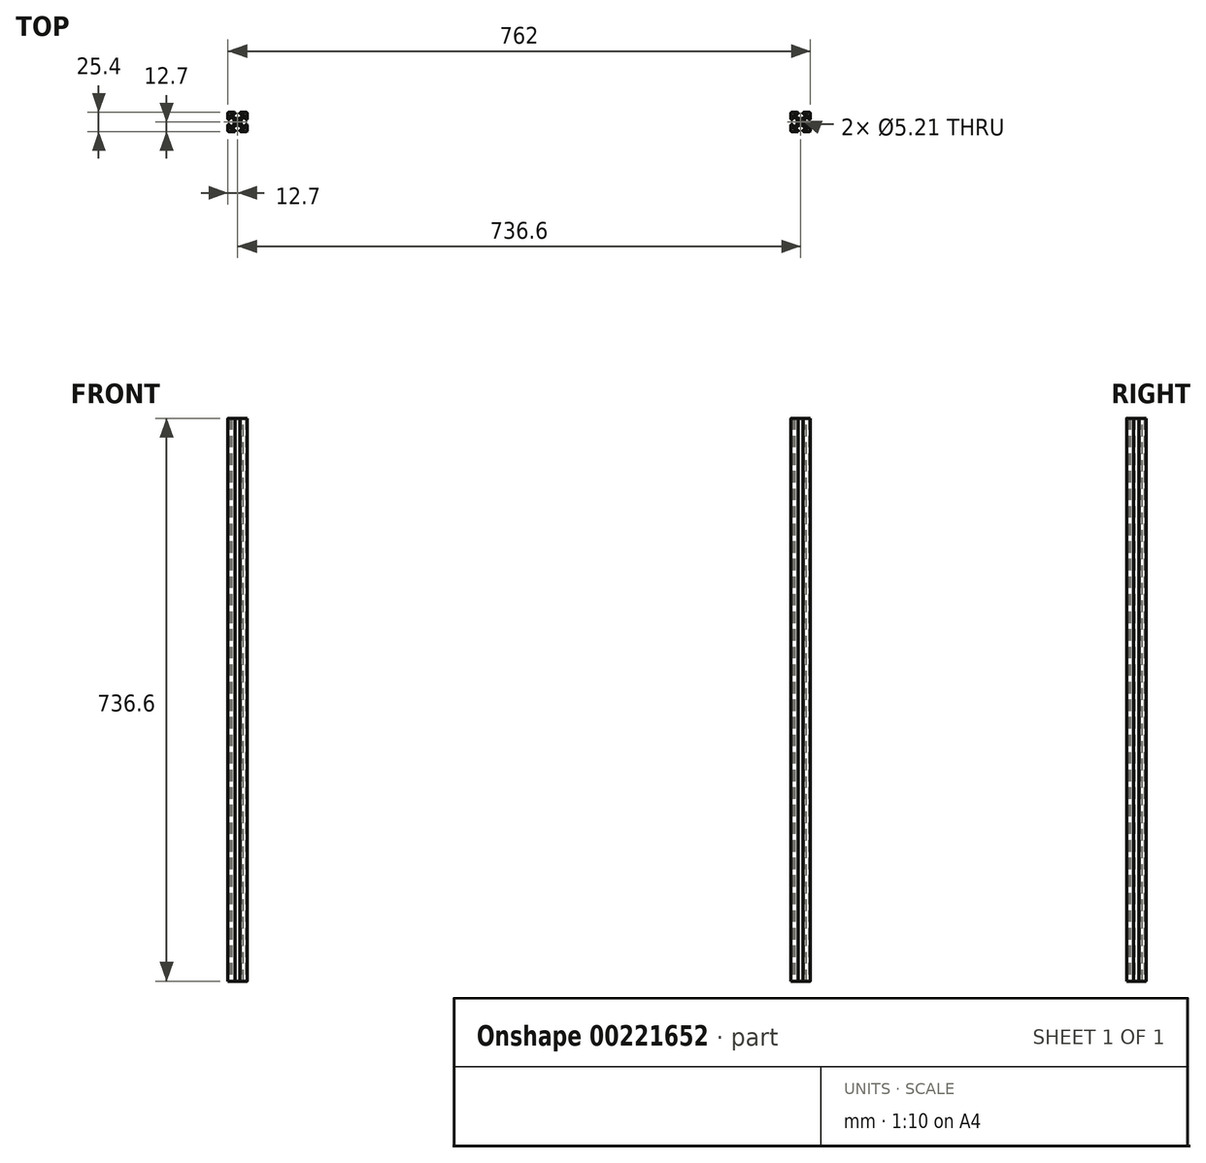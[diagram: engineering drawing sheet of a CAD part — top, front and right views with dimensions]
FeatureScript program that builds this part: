
annotation { "Feature Type Name" : "Feature", "Feature Type Description" : "" }
export const myFeature = defineFeature(function(context is Context, id is Id, definition is map)
    precondition{}
    {
        {
            var Q0;
            Q0=qCreatedBy(makeId("Top.planeOp"),FACE);
            var sketch = newSketch(context, id + "F0", { "sketchPlane" : qUnion([Q0])});
            skLineSegment(sketch, "E0.bottom", {"start": v(12.7, 12.7) * mm, "end": v(-12.7, 12.7) * mm});
            skLineSegment(sketch, "E0.top", {"start": v(12.7, -12.7) * mm, "end": v(-12.7, -12.7) * mm});
            skLineSegment(sketch, "E0.left", {"start": v(12.7, 12.7) * mm, "end": v(12.7, -12.7) * mm});
            skLineSegment(sketch, "E0.right", {"start": v(-12.7, 12.7) * mm, "end": v(-12.7, -12.7) * mm});
            skPoint(sketch, "E0.middle", {"position": v(0, 0) * mm});
            skCircle(sketch, "E1", {"center": v(0, 0) * mm, "radius": 2.6 * mm});
            skLineSegment(sketch, "E2", {"start": v(-12.7, 12.7) * mm, "end": v(12.7, -12.7) * mm, "construction": true});
            skLineSegment(sketch, "E3", {"start": v(0, 12.7) * mm, "end": v(0, -12.7) * mm, "construction": true});
            skLineSegment(sketch, "E4", {"start": v(-12.7, -12.7) * mm, "end": v(12.7, 12.7) * mm, "construction": true});
            skLineSegment(sketch, "E5", {"start": v(-8.78, 10.34) * mm, "end": v(-2.95, 4.5) * mm});
            skLineSegment(sketch, "E6.MirrorCS", {"start": v(8.78, 10.34) * mm, "end": v(2.95, 4.5) * mm});
            skLineSegment(sketch, "E7", {"start": v(-2.95, 4.5) * mm, "end": v(2.95, 4.5) * mm});
            skLineSegment(sketch, "E8.bottom", {"start": v(-3.24, 14.9) * mm, "end": v(3.24, 14.9) * mm});
            skLineSegment(sketch, "E8.left", {"start": v(-3.24, 14.9) * mm, "end": v(-3.24, 10.34) * mm});
            skLineSegment(sketch, "E8.right", {"start": v(3.24, 14.9) * mm, "end": v(3.24, 10.34) * mm});
            skLineSegment(sketch, "E9", {"start": v(-8.78, 10.34) * mm, "end": v(-3.24, 10.34) * mm});
            skLineSegment(sketch, "E10", {"start": v(3.24, 10.34) * mm, "end": v(8.78, 10.34) * mm});
            skLineSegment(sketch, "E11.MirrorCS", {"start": v(-10.34, 8.78) * mm, "end": v(-4.5, 2.95) * mm});
            skLineSegment(sketch, "E12.MirrorCS", {"start": v(-10.34, 8.78) * mm, "end": v(-10.34, 3.24) * mm});
            skLineSegment(sketch, "E13.MirrorCS", {"start": v(-14.9, 3.24) * mm, "end": v(-10.34, 3.24) * mm});
            skLineSegment(sketch, "E14.MirrorCS", {"start": v(-14.9, 3.24) * mm, "end": v(-14.9, -3.24) * mm});
            skLineSegment(sketch, "E15.MirrorCS", {"start": v(-14.9, -3.24) * mm, "end": v(-10.34, -3.24) * mm});
            skLineSegment(sketch, "E16.MirrorCS", {"start": v(-10.34, -3.24) * mm, "end": v(-10.34, -8.78) * mm});
            skLineSegment(sketch, "E17.MirrorCS", {"start": v(-10.34, -8.78) * mm, "end": v(-4.5, -2.95) * mm});
            skLineSegment(sketch, "E18.MirrorCS", {"start": v(-4.5, 2.95) * mm, "end": v(-4.5, -2.95) * mm});
            skLineSegment(sketch, "E19.MirrorCS", {"start": v(10.34, 8.78) * mm, "end": v(4.5, 2.95) * mm});
            skLineSegment(sketch, "E20.MirrorCS", {"start": v(4.5, -2.95) * mm, "end": v(4.5, 2.95) * mm});
            skLineSegment(sketch, "E21.MirrorCS", {"start": v(10.34, -8.78) * mm, "end": v(4.5, -2.95) * mm});
            skLineSegment(sketch, "E22.MirrorCS", {"start": v(10.34, -8.78) * mm, "end": v(10.34, -3.24) * mm});
            skLineSegment(sketch, "E23.MirrorCS", {"start": v(14.9, -3.24) * mm, "end": v(10.34, -3.24) * mm});
            skLineSegment(sketch, "E24.MirrorCS", {"start": v(14.9, -3.24) * mm, "end": v(14.9, 3.24) * mm});
            skLineSegment(sketch, "E25.MirrorCS", {"start": v(14.9, 3.24) * mm, "end": v(10.34, 3.24) * mm});
            skLineSegment(sketch, "E26.MirrorCS", {"start": v(10.34, 3.24) * mm, "end": v(10.34, 8.78) * mm});
            skLineSegment(sketch, "E27", {"start": v(-12.7, 0) * mm, "end": v(12.7, 0) * mm, "construction": true});
            skLineSegment(sketch, "E28.MirrorCS", {"start": v(-8.78, -10.34) * mm, "end": v(-2.95, -4.5) * mm});
            skLineSegment(sketch, "E29.MirrorCS", {"start": v(-8.78, -10.34) * mm, "end": v(-3.24, -10.34) * mm});
            skLineSegment(sketch, "E30.MirrorCS", {"start": v(-3.24, -14.9) * mm, "end": v(-3.24, -10.34) * mm});
            skLineSegment(sketch, "E31.MirrorCS", {"start": v(-3.24, -14.9) * mm, "end": v(3.24, -14.9) * mm});
            skLineSegment(sketch, "E32.MirrorCS", {"start": v(3.24, -14.9) * mm, "end": v(3.24, -10.34) * mm});
            skLineSegment(sketch, "E33.MirrorCS", {"start": v(3.24, -10.34) * mm, "end": v(8.78, -10.34) * mm});
            skLineSegment(sketch, "E34.MirrorCS", {"start": v(8.78, -10.34) * mm, "end": v(2.95, -4.5) * mm});
            skLineSegment(sketch, "E35.MirrorCS", {"start": v(-2.95, -4.5) * mm, "end": v(2.95, -4.5) * mm});
            skSolve(sketch);
        }
        {
            var Q0;
            Q0=makeQuery(id+"F0.imprint","IMPRINT",FACE,{"disambiguationData":[TD([[makeQuery(id+"F0.imprint","IMPRINT",EDGE,{"derivedFrom":sQuery(id+"F0.wireOp",EDGE,"E1")}),-1.0]])]});
            extrude(context, id + "F1", {"entities" : qUnion([Q0]), "depth" : 736.6 * mm});
        }
        {
            var Q0;
            Q0=makeQuery(id+"F1.opExtrude","SWEPT_EDGE",EDGE,{"disambiguationData":[OSD([sQuery(id+"F0.wireOp",EDGE,"E0.bottom"),sQuery(id+"F0.wireOp",EDGE,"E8.right")])]});
            var Q1;
            Q1=makeQuery(id+"F1.opExtrude","SWEPT_EDGE",EDGE,{"disambiguationData":[OSD([sQuery(id+"F0.wireOp",EDGE,"E8.right"),sQuery(id+"F0.wireOp",EDGE,"E10")])]});
            var Q2;
            Q2=makeQuery(id+"F1.opExtrude","SWEPT_EDGE",EDGE,{"disambiguationData":[OSD([sQuery(id+"F0.wireOp",EDGE,"E0.bottom"),sQuery(id+"F0.wireOp",EDGE,"E8.left")])]});
            var Q3;
            Q3=makeQuery(id+"F1.opExtrude","SWEPT_EDGE",EDGE,{"disambiguationData":[OSD([sQuery(id+"F0.wireOp",EDGE,"E0.right"),sQuery(id+"F0.wireOp",EDGE,"E13.MirrorCS")])]});
            var Q4;
            Q4=makeQuery(id+"F1.opExtrude","SWEPT_EDGE",EDGE,{"disambiguationData":[OSD([sQuery(id+"F0.wireOp",EDGE,"E8.left"),sQuery(id+"F0.wireOp",EDGE,"E9")])]});
            var Q5;
            Q5=makeQuery(id+"F1.opExtrude","SWEPT_EDGE",EDGE,{"disambiguationData":[OSD([sQuery(id+"F0.wireOp",EDGE,"E12.MirrorCS"),sQuery(id+"F0.wireOp",EDGE,"E13.MirrorCS")])]});
            var Q6;
            Q6=makeQuery(id+"F1.opExtrude","SWEPT_EDGE",EDGE,{"disambiguationData":[OSD([sQuery(id+"F0.wireOp",EDGE,"E0.left"),sQuery(id+"F0.wireOp",EDGE,"E25.MirrorCS")])]});
            var Q7;
            Q7=makeQuery(id+"F1.opExtrude","SWEPT_EDGE",EDGE,{"disambiguationData":[OSD([sQuery(id+"F0.wireOp",EDGE,"E25.MirrorCS"),sQuery(id+"F0.wireOp",EDGE,"E26.MirrorCS")])]});
            var Q8;
            Q8=makeQuery(id+"F1.opExtrude","SWEPT_EDGE",EDGE,{"disambiguationData":[OSD([sQuery(id+"F0.wireOp",EDGE,"E0.left"),sQuery(id+"F0.wireOp",EDGE,"E23.MirrorCS")])]});
            var Q9;
            Q9=makeQuery(id+"F1.opExtrude","SWEPT_EDGE",EDGE,{"disambiguationData":[OSD([sQuery(id+"F0.wireOp",EDGE,"E22.MirrorCS"),sQuery(id+"F0.wireOp",EDGE,"E23.MirrorCS")])]});
            var Q10;
            Q10=makeQuery(id+"F1.opExtrude","SWEPT_EDGE",EDGE,{"disambiguationData":[OSD([sQuery(id+"F0.wireOp",EDGE,"E32.MirrorCS"),sQuery(id+"F0.wireOp",EDGE,"E33.MirrorCS")])]});
            var Q11;
            Q11=makeQuery(id+"F1.opExtrude","SWEPT_EDGE",EDGE,{"disambiguationData":[OSD([sQuery(id+"F0.wireOp",EDGE,"E29.MirrorCS"),sQuery(id+"F0.wireOp",EDGE,"E30.MirrorCS")])]});
            var Q12;
            Q12=makeQuery(id+"F1.opExtrude","SWEPT_EDGE",EDGE,{"disambiguationData":[OSD([sQuery(id+"F0.wireOp",EDGE,"E15.MirrorCS"),sQuery(id+"F0.wireOp",EDGE,"E16.MirrorCS")])]});
            var Q13;
            Q13=makeQuery(id+"F1.opExtrude","SWEPT_EDGE",EDGE,{"disambiguationData":[OSD([sQuery(id+"F0.wireOp",EDGE,"E0.right"),sQuery(id+"F0.wireOp",EDGE,"E15.MirrorCS")])]});
            var Q14;
            Q14=makeQuery(id+"F1.opExtrude","SWEPT_EDGE",EDGE,{"disambiguationData":[OSD([sQuery(id+"F0.wireOp",EDGE,"E0.top"),sQuery(id+"F0.wireOp",EDGE,"E30.MirrorCS")])]});
            var Q15;
            Q15=makeQuery(id+"F1.opExtrude","SWEPT_EDGE",EDGE,{"disambiguationData":[OSD([sQuery(id+"F0.wireOp",EDGE,"E0.top"),sQuery(id+"F0.wireOp",EDGE,"E32.MirrorCS")])]});
            fillet(context, id + "F2", {"entities" : qUnion([Q0, Q1, Q2, Q3, Q4, Q5, Q6, Q7, Q8, Q9, Q10, Q11, Q12, Q13, Q14, Q15]), "radius" : 1.18 * mm, "tangentPropagation" : true, "allowEdgeOverflow" : false});
        }
        {
            var Q0;
            Q0=makeQuery(id+"F1.opExtrude","SWEPT_EDGE",EDGE,{"disambiguationData":[OSD([sQuery(id+"F0.wireOp",EDGE,"E6.MirrorCS"),sQuery(id+"F0.wireOp",EDGE,"E7")])]});
            var Q1;
            Q1=makeQuery(id+"F1.opExtrude","SWEPT_EDGE",EDGE,{"disambiguationData":[OSD([sQuery(id+"F0.wireOp",EDGE,"E5"),sQuery(id+"F0.wireOp",EDGE,"E7")])]});
            var Q2;
            Q2=makeQuery(id+"F1.opExtrude","SWEPT_EDGE",EDGE,{"disambiguationData":[OSD([sQuery(id+"F0.wireOp",EDGE,"E20.MirrorCS"),sQuery(id+"F0.wireOp",EDGE,"E21.MirrorCS")])]});
            var Q3;
            Q3=makeQuery(id+"F1.opExtrude","SWEPT_EDGE",EDGE,{"disambiguationData":[OSD([sQuery(id+"F0.wireOp",EDGE,"E19.MirrorCS"),sQuery(id+"F0.wireOp",EDGE,"E20.MirrorCS")])]});
            var Q4;
            Q4=makeQuery(id+"F1.opExtrude","SWEPT_EDGE",EDGE,{"disambiguationData":[OSD([sQuery(id+"F0.wireOp",EDGE,"E34.MirrorCS"),sQuery(id+"F0.wireOp",EDGE,"E35.MirrorCS")])]});
            var Q5;
            Q5=makeQuery(id+"F1.opExtrude","SWEPT_EDGE",EDGE,{"disambiguationData":[OSD([sQuery(id+"F0.wireOp",EDGE,"E28.MirrorCS"),sQuery(id+"F0.wireOp",EDGE,"E35.MirrorCS")])]});
            var Q6;
            Q6=makeQuery(id+"F1.opExtrude","SWEPT_EDGE",EDGE,{"disambiguationData":[OSD([sQuery(id+"F0.wireOp",EDGE,"E17.MirrorCS"),sQuery(id+"F0.wireOp",EDGE,"E18.MirrorCS")])]});
            var Q7;
            Q7=makeQuery(id+"F1.opExtrude","SWEPT_EDGE",EDGE,{"disambiguationData":[OSD([sQuery(id+"F0.wireOp",EDGE,"E11.MirrorCS"),sQuery(id+"F0.wireOp",EDGE,"E18.MirrorCS")])]});
            fillet(context, id + "F3", {"entities" : qUnion([Q0, Q1, Q2, Q3, Q4, Q5, Q6, Q7]), "radius" : 5.08 * mm, "tangentPropagation" : true, "allowEdgeOverflow" : false});
        }
        {
            var Q0;
            Q0=makeQuery(id+"F1.opExtrude","SWEPT_EDGE",EDGE,{"disambiguationData":[OSD([sQuery(id+"F0.wireOp",EDGE,"E6.MirrorCS"),sQuery(id+"F0.wireOp",EDGE,"E10")])]});
            var Q1;
            Q1=makeQuery(id+"F1.opExtrude","SWEPT_EDGE",EDGE,{"disambiguationData":[OSD([sQuery(id+"F0.wireOp",EDGE,"E5"),sQuery(id+"F0.wireOp",EDGE,"E9")])]});
            var Q2;
            Q2=makeQuery(id+"F1.opExtrude","SWEPT_EDGE",EDGE,{"disambiguationData":[OSD([sQuery(id+"F0.wireOp",EDGE,"E11.MirrorCS"),sQuery(id+"F0.wireOp",EDGE,"E12.MirrorCS")])]});
            var Q3;
            Q3=makeQuery(id+"F1.opExtrude","SWEPT_EDGE",EDGE,{"disambiguationData":[OSD([sQuery(id+"F0.wireOp",EDGE,"E16.MirrorCS"),sQuery(id+"F0.wireOp",EDGE,"E17.MirrorCS")])]});
            var Q4;
            Q4=makeQuery(id+"F1.opExtrude","SWEPT_EDGE",EDGE,{"disambiguationData":[OSD([sQuery(id+"F0.wireOp",EDGE,"E28.MirrorCS"),sQuery(id+"F0.wireOp",EDGE,"E29.MirrorCS")])]});
            var Q5;
            Q5=makeQuery(id+"F1.opExtrude","SWEPT_EDGE",EDGE,{"disambiguationData":[OSD([sQuery(id+"F0.wireOp",EDGE,"E33.MirrorCS"),sQuery(id+"F0.wireOp",EDGE,"E34.MirrorCS")])]});
            var Q6;
            Q6=makeQuery(id+"F1.opExtrude","SWEPT_EDGE",EDGE,{"disambiguationData":[OSD([sQuery(id+"F0.wireOp",EDGE,"E21.MirrorCS"),sQuery(id+"F0.wireOp",EDGE,"E22.MirrorCS")])]});
            var Q7;
            Q7=makeQuery(id+"F1.opExtrude","SWEPT_EDGE",EDGE,{"disambiguationData":[OSD([sQuery(id+"F0.wireOp",EDGE,"E19.MirrorCS"),sQuery(id+"F0.wireOp",EDGE,"E26.MirrorCS")])]});
            fillet(context, id + "F4", {"entities" : qUnion([Q0, Q1, Q2, Q3, Q4, Q5, Q6, Q7]), "radius" : 0.76 * mm, "tangentPropagation" : true, "allowEdgeOverflow" : false});
        }
        {
            var Q0;
            Q0=makeQuery(id+"F1.opExtrude","SWEPT_EDGE",EDGE,{"disambiguationData":[OSD([sQuery(id+"F0.wireOp",EDGE,"E0.top"),sQuery(id+"F0.wireOp",EDGE,"E0.right")])]});
            var Q1;
            Q1=makeQuery(id+"F1.opExtrude","SWEPT_EDGE",EDGE,{"disambiguationData":[OSD([sQuery(id+"F0.wireOp",EDGE,"E0.top"),sQuery(id+"F0.wireOp",EDGE,"E0.left")])]});
            var Q2;
            Q2=makeQuery(id+"F1.opExtrude","SWEPT_EDGE",EDGE,{"disambiguationData":[OSD([sQuery(id+"F0.wireOp",EDGE,"E0.bottom"),sQuery(id+"F0.wireOp",EDGE,"E0.left")])]});
            var Q3;
            Q3=makeQuery(id+"F1.opExtrude","SWEPT_EDGE",EDGE,{"disambiguationData":[OSD([sQuery(id+"F0.wireOp",EDGE,"E0.bottom"),sQuery(id+"F0.wireOp",EDGE,"E0.right")])]});
            fillet(context, id + "F5", {"entities" : qUnion([Q0, Q1, Q2, Q3]), "radius" : 1.27 * mm, "tangentPropagation" : true, "allowEdgeOverflow" : false});
        }
        {
            var Q0;
            Q0=makeQuery(id+"F1.opExtrude","SWEPT_BODY",BODY,{"disambiguationData":[OSD([sQuery(id+"F0.wireOp",EDGE,"E0.bottom"),sQuery(id+"F0.wireOp",EDGE,"E0.top"),sQuery(id+"F0.wireOp",EDGE,"E0.left"),sQuery(id+"F0.wireOp",EDGE,"E0.right"),sQuery(id+"F0.wireOp",EDGE,"E1"),sQuery(id+"F0.wireOp",EDGE,"E5"),sQuery(id+"F0.wireOp",EDGE,"E6.MirrorCS"),sQuery(id+"F0.wireOp",EDGE,"E7"),sQuery(id+"F0.wireOp",EDGE,"E8.left"),sQuery(id+"F0.wireOp",EDGE,"E8.right"),sQuery(id+"F0.wireOp",EDGE,"E9"),sQuery(id+"F0.wireOp",EDGE,"E10"),sQuery(id+"F0.wireOp",EDGE,"E11.MirrorCS"),sQuery(id+"F0.wireOp",EDGE,"E12.MirrorCS"),sQuery(id+"F0.wireOp",EDGE,"E13.MirrorCS"),sQuery(id+"F0.wireOp",EDGE,"E15.MirrorCS"),sQuery(id+"F0.wireOp",EDGE,"E16.MirrorCS"),sQuery(id+"F0.wireOp",EDGE,"E17.MirrorCS"),sQuery(id+"F0.wireOp",EDGE,"E18.MirrorCS"),sQuery(id+"F0.wireOp",EDGE,"E19.MirrorCS"),sQuery(id+"F0.wireOp",EDGE,"E20.MirrorCS"),sQuery(id+"F0.wireOp",EDGE,"E21.MirrorCS"),sQuery(id+"F0.wireOp",EDGE,"E22.MirrorCS"),sQuery(id+"F0.wireOp",EDGE,"E23.MirrorCS"),sQuery(id+"F0.wireOp",EDGE,"E25.MirrorCS"),sQuery(id+"F0.wireOp",EDGE,"E26.MirrorCS"),sQuery(id+"F0.wireOp",EDGE,"E28.MirrorCS"),sQuery(id+"F0.wireOp",EDGE,"E29.MirrorCS"),sQuery(id+"F0.wireOp",EDGE,"E30.MirrorCS"),sQuery(id+"F0.wireOp",EDGE,"E32.MirrorCS"),sQuery(id+"F0.wireOp",EDGE,"E33.MirrorCS"),sQuery(id+"F0.wireOp",EDGE,"E34.MirrorCS"),sQuery(id+"F0.wireOp",EDGE,"E35.MirrorCS")])]});
            var Q1;
            {var subQ0=sQuery(id+"F0.wireOp",EDGE,"E0.top");Q1=makeQuery(id+"F1.opExtrude","CAP_EDGE",EDGE,{"disambiguationData":[OSD([subQ0]),TDD([makeQuery(id+"F0.imprint","IMPRINT",EDGE,{"disambiguationData":[TD([[makeQuery(id+"F0.imprint","INTERSECT",VERTEX,{"derivedFrom":[subQ0,sQuery(id+"F0.wireOp",EDGE,"E0.right")]}),1.0]])],"derivedFrom":subQ0})])],"isStart":true});}
            transform(context, id + "F6", {"entities" : qUnion([Q0]), "transformType" : TransformType.TRANSLATION_3D, "dx" : 736.6 * mm, "dy" : 0 * mm, "dz" : 0 * mm, "makeCopy" : true});
        }
    });
